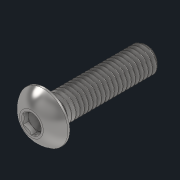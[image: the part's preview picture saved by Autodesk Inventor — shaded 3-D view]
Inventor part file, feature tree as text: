
AUTODESK INVENTOR PART (.ipt)
format: ipt  version: 2021 (Build 250183000, 183)  size: 615,424 bytes
history: native  units: in
note: dims shown in document units (in); Inventor stores cm internally (conversion verified against a paired STEP export)
features: revolve x1
ambient origin geometry x8: Origin, YZ Plane, XZ Plane, XY Plane, X Axis, Y Axis, Z Axis, Center Point
bodies: Solid1 (feature_tree)
feature tree (1):
  revolve  "Revolve2"  [1 undecoded]
note: 1 required parameter value undecoded (feature->parameter linkage not recoverable at this tier; creation-order binding heuristic only, values carry confidence <= 0.55)
